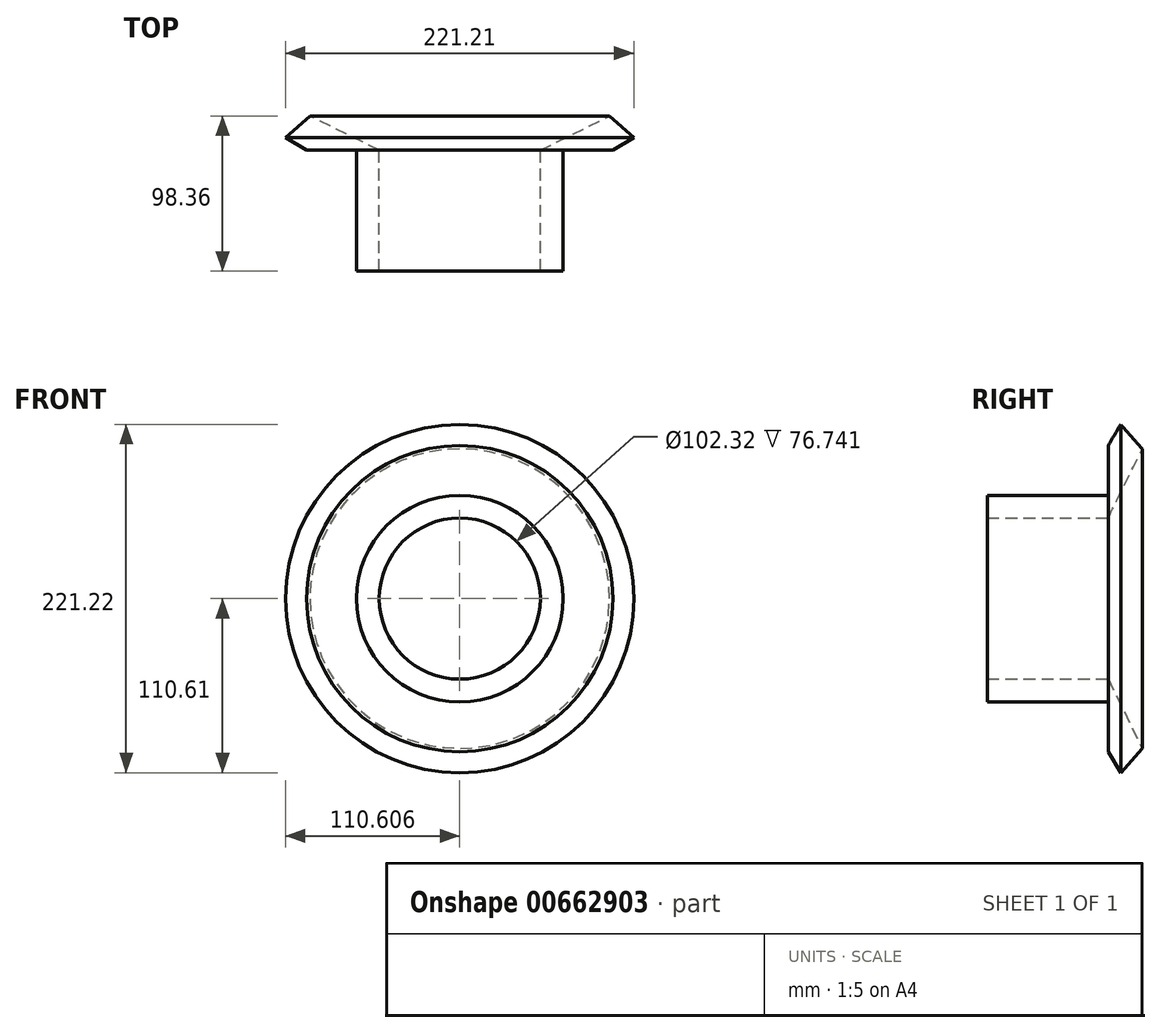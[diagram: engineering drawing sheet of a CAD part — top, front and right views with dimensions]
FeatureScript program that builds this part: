
annotation { "Feature Type Name" : "Feature", "Feature Type Description" : "" }
export const myFeature = defineFeature(function(context is Context, id is Id, definition is map)
    precondition{}
    {
        {
            var Q0;
            Q0=qCreatedBy(makeId("Top.planeOp"),FACE);
            var sketch = newSketch(context, id + "F0", { "sketchPlane" : qUnion([Q0])});
            skLineSegment(sketch, "E0", {"start": v(-105.38, 54.58) * mm, "end": v(-105.38, -59.27) * mm, "construction": true});
            skLineSegment(sketch, "E1", {"start": v(-10.27, 38.37) * mm, "end": v(-54.22, 16.75) * mm});
            skLineSegment(sketch, "E2", {"start": v(-54.22, 16.75) * mm, "end": v(-54.22, -59.99) * mm});
            skLineSegment(sketch, "E3", {"start": v(-54.22, -59.99) * mm, "end": v(-39.81, -59.99) * mm});
            skLineSegment(sketch, "E4", {"start": v(-39.81, -59.99) * mm, "end": v(-39.81, 16.75) * mm});
            skLineSegment(sketch, "E5", {"start": v(-39.81, 16.75) * mm, "end": v(-8.1, 16.75) * mm});
            skLineSegment(sketch, "E6", {"start": v(-8.1, 16.75) * mm, "end": v(5.22, 24.68) * mm});
            skLineSegment(sketch, "E7", {"start": v(5.22, 24.68) * mm, "end": v(-10.27, 38.37) * mm});
            skSolve(sketch);
        }
        {
            var Q0;
            Q0=makeQuery(id+"F0.imprint","IMPRINT",FACE,{"disambiguationData":[TD([[makeQuery(id+"F0.imprint","IMPRINT",EDGE,{"derivedFrom":sQuery(id+"F0.wireOp",EDGE,"E1")}),1.0]])]});
            var Q1;
            Q1=sQuery(id+"F0.wireOp",EDGE,"E0");
            revolve(context, id + "F1", {"entities" : qUnion([Q0]), "axis" : qUnion([Q1]), "revolveType" : RevolveType.FULL});
        }
    });
